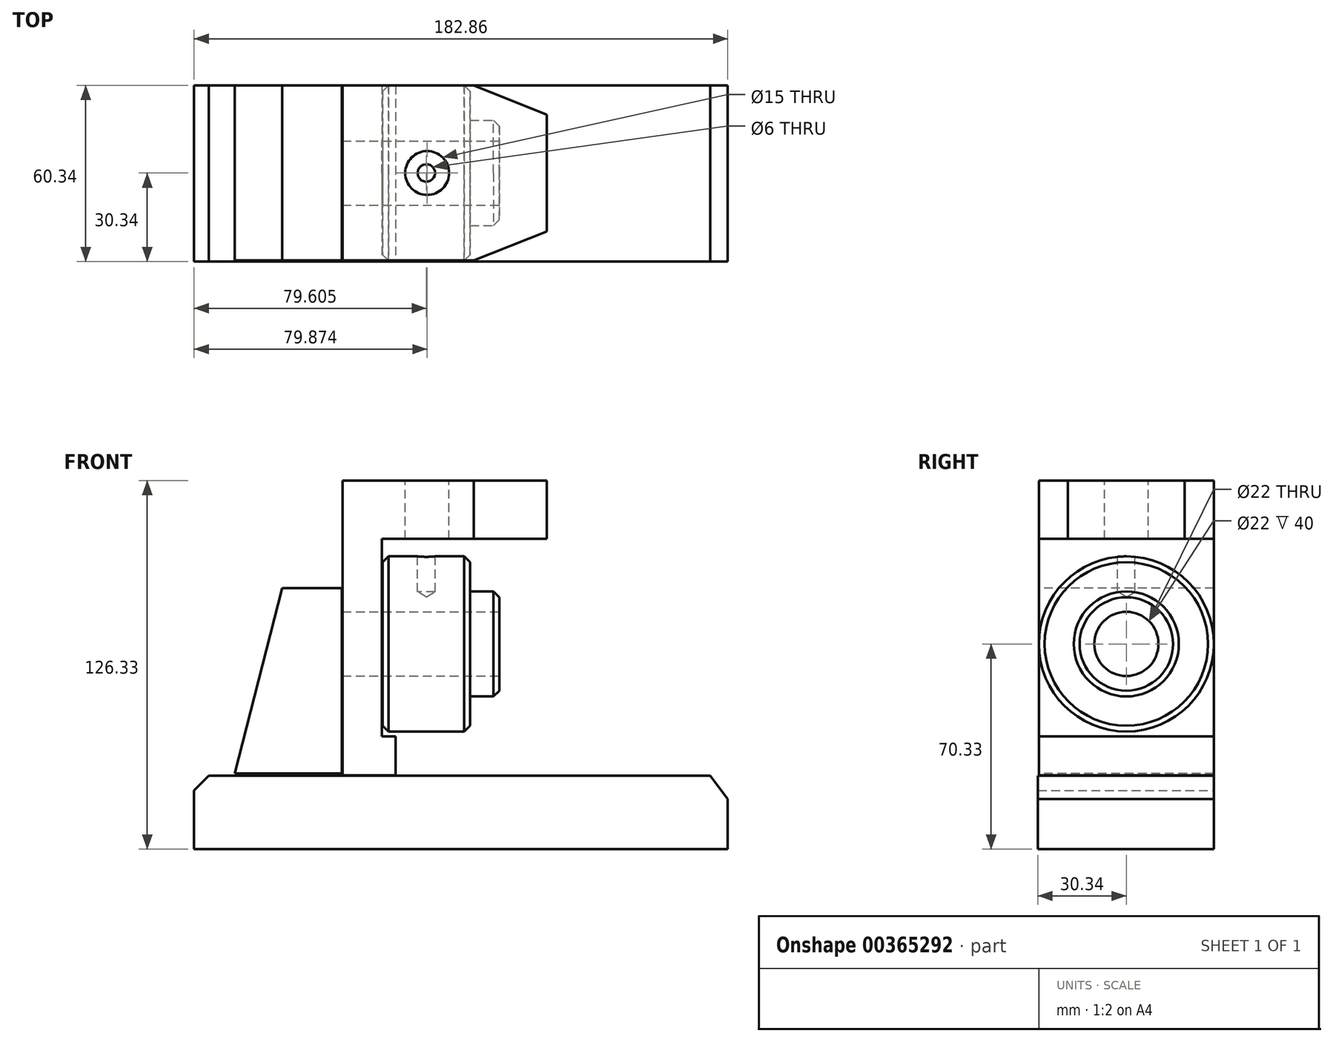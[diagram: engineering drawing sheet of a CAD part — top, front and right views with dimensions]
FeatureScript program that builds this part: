
annotation { "Feature Type Name" : "Feature", "Feature Type Description" : "" }
export const myFeature = defineFeature(function(context is Context, id is Id, definition is map)
    precondition{}
    {
        {
            var Q0;
            Q0=qCreatedBy(makeId("Front.planeOp"),FACE);
            var sketch = newSketch(context, id + "F0", { "sketchPlane" : qUnion([Q0])});
            skLineSegment(sketch, "E0", {"start": v(-19, 18) * mm, "end": v(-29, 18) * mm});
            skLineSegment(sketch, "E1", {"start": v(-29, 18) * mm, "end": v(-29, 30) * mm});
            skLineSegment(sketch, "E2", {"start": v(-29, 30) * mm, "end": v(-59, 30) * mm});
            skPoint(sketch, "E3", {"position": v(0, 0) * mm});
            skLineSegment(sketch, "E4", {"start": v(-19, 18) * mm, "end": v(-19, 11) * mm});
            skLineSegment(sketch, "E5", {"start": v(-19, 11) * mm, "end": v(-59, 11) * mm});
            skLineSegment(sketch, "E6", {"start": v(-59, 11) * mm, "end": v(-59, 30) * mm});
            skLineSegment(sketch, "E7", {"start": v(0, 0) * mm, "end": v(-59, 0) * mm, "construction": true});
            skSolve(sketch);
        }
        {
            var Q0;
            Q0=makeQuery(id+"F0.imprint","IMPRINT",FACE,{"disambiguationData":[TD([[makeQuery(id+"F0.imprint","IMPRINT",EDGE,{"derivedFrom":sQuery(id+"F0.wireOp",EDGE,"E0")}),1.0]])]});
            var Q1;
            Q1=sQuery(id+"F0.wireOp",EDGE,"E7");
            revolve(context, id + "F1", {"entities" : qUnion([Q0]), "axis" : qUnion([Q1]), "revolveType" : RevolveType.FULL});
        }
        {
            var Q0;
            Q0=makeQuery(id+"F1.opRevolve","SWEPT_EDGE",EDGE,{"disambiguationData":[OSD([sQuery(id+"F0.wireOp",EDGE,"E0"),sQuery(id+"F0.wireOp",EDGE,"E4")])]});
            var Q1;
            Q1=makeQuery(id+"F1.opRevolve","SWEPT_EDGE",EDGE,{"disambiguationData":[OSD([sQuery(id+"F0.wireOp",EDGE,"E1"),sQuery(id+"F0.wireOp",EDGE,"E2")])]});
            var Q2;
            Q2=makeQuery(id+"F1.opRevolve","SWEPT_EDGE",EDGE,{"disambiguationData":[OSD([sQuery(id+"F0.wireOp",EDGE,"E2"),sQuery(id+"F0.wireOp",EDGE,"E6")])]});
            chamfer(context, id + "F2", {"entities" : qUnion([Q0, Q1, Q2]), "width" : 2 * mm, "tangentPropagation" : true});
        }
        {
            var Q0;
            Q0=qCreatedBy(makeId("Top.planeOp"),FACE);
            cPlane(context, id + "F3", {"entities" : qUnion([Q0]), "cplaneType" : CPlaneType.OFFSET, "offset" : 30 * mm, "width" : 150 * mm, "height" : 150 * mm});
        }
        {
            var Q0;
            Q0=qCreatedBy(id+"F3.planeOp",FACE);
            var sketch = newSketch(context, id + "F4", { "sketchPlane" : qUnion([Q0])});
            skCircle(sketch, "E8", {"center": v(-44, 0) * mm, "radius": 3 * mm});
            skSolve(sketch);
        }
        {
            var Q0;
            Q0=sQuery(id+"F4.wireOp",VERTEX,"E8.center");
            var Q1;
            Q1=makeQuery(id+"F1.opRevolve","SWEPT_BODY",BODY,{"disambiguationData":[OSD([sQuery(id+"F0.wireOp",EDGE,"E0"),sQuery(id+"F0.wireOp",EDGE,"E1"),sQuery(id+"F0.wireOp",EDGE,"E2"),sQuery(id+"F0.wireOp",EDGE,"E4"),sQuery(id+"F0.wireOp",EDGE,"E5"),sQuery(id+"F0.wireOp",EDGE,"E6")])]});
            hole(context, id + "F5", {"style" : HoleStyle.SIMPLE, "endStyle" : HoleEndStyle.BLIND, "holeDiameter" : 6 * mm, "holeDepth" : 12 * mm, "isTappedThrough" : true, "tappedDepth" : 12 * mm, "tapClearance" : 3, "locations" : qUnion([Q0]), "scope" : qUnion([Q1])});
        }
        {
            var Q0;
            Q0=qCreatedBy(makeId("Right.planeOp"),FACE);
            cPlane(context, id + "F6", {"entities" : qUnion([Q0]), "cplaneType" : CPlaneType.OFFSET, "offset" : 59 * mm, "oppositeDirection" : true, "width" : 150 * mm, "height" : 150 * mm});
        }
        {
            var Q0;
            Q0=qCreatedBy(makeId("Front.planeOp"),FACE);
            cPlane(context, id + "F7", {"entities" : qUnion([Q0]), "cplaneType" : CPlaneType.OFFSET, "offset" : 30 * mm, "width" : 150 * mm, "height" : 150 * mm});
        }
        {
            var Q0;
            Q0=qCreatedBy(id+"F7.planeOp",FACE);
            var sketch = newSketch(context, id + "F8", { "sketchPlane" : qUnion([Q0])});
            skLineSegment(sketch, "E9", {"start": v(-59.2, 36) * mm, "end": v(-59.2, -31.66) * mm});
            skLineSegment(sketch, "E10", {"start": v(-59.2, -31.66) * mm, "end": v(-54.5, -31.66) * mm});
            skLineSegment(sketch, "E11", {"start": v(-54.5, -31.66) * mm, "end": v(-54.5, -45) * mm});
            skLineSegment(sketch, "E12", {"start": v(-54.5, -45) * mm, "end": v(-72.74, -45) * mm});
            skLineSegment(sketch, "E13", {"start": v(-72.74, -45) * mm, "end": v(-72.74, 56) * mm});
            skLineSegment(sketch, "E14", {"start": v(-72.74, 56) * mm, "end": v(-2.74, 56) * mm});
            skLineSegment(sketch, "E15", {"start": v(-2.74, 56) * mm, "end": v(-2.74, 36) * mm});
            skLineSegment(sketch, "E16", {"start": v(-2.74, 36) * mm, "end": v(-59.2, 36) * mm});
            skSolve(sketch);
        }
        {
            var Q0;
            Q0=makeQuery(id+"F8.imprint","IMPRINT",FACE,{"disambiguationData":[TD([[makeQuery(id+"F8.imprint","IMPRINT",EDGE,{"derivedFrom":sQuery(id+"F8.wireOp",EDGE,"E9")}),-1.0]])]});
            extrude(context, id + "F9", {"entities" : qUnion([Q0]), "oppositeDirection" : true, "depth" : 60 * mm});
        }
        {
            var Q0;
            Q0=makeQuery(id+"F9.opExtrude","CAP_EDGE",EDGE,{"disambiguationData":[OSD([sQuery(id+"F8.wireOp",EDGE,"E15")])],"isStart":false});
            var Q1;
            Q1=makeQuery(id+"F9.opExtrude","CAP_EDGE",EDGE,{"disambiguationData":[OSD([sQuery(id+"F8.wireOp",EDGE,"E15")])],"isStart":true});
            chamfer(context, id + "F10", {"entities" : qUnion([Q0, Q1]), "chamferType" : ChamferType.TWO_OFFSETS, "width1" : 25 * mm, "oppositeDirection" : false, "width2" : 10 * mm, "tangentPropagation" : true});
        }
        {
            var Q0;
            Q0=qCreatedBy(id+"F3.planeOp",FACE);
            cPlane(context, id + "F11", {"entities" : qUnion([Q0]), "cplaneType" : CPlaneType.OFFSET, "offset" : 25 * mm, "width" : 150 * mm, "height" : 150 * mm});
        }
        {
            var Q0;
            Q0=makeQuery(id+"F9.opExtrude","SWEPT_FACE",FACE,{"disambiguationData":[OSD([sQuery(id+"F8.wireOp",EDGE,"E14")])]});
            var sketch = newSketch(context, id + "F12", { "sketchPlane" : qUnion([Q0])});
            skPoint(sketch, "E17", {"position": v(-43.74, 0) * mm});
            skSolve(sketch);
        }
        {
            var Q0;
            Q0=sQuery(id+"F12.wireOp",VERTEX,"E17");
            var Q1;
            Q1=makeQuery(id+"F9.opExtrude","SWEPT_BODY",BODY,{"disambiguationData":[OSD([sQuery(id+"F8.wireOp",EDGE,"E9"),sQuery(id+"F8.wireOp",EDGE,"E10"),sQuery(id+"F8.wireOp",EDGE,"E11"),sQuery(id+"F8.wireOp",EDGE,"E12"),sQuery(id+"F8.wireOp",EDGE,"E13"),sQuery(id+"F8.wireOp",EDGE,"E14"),sQuery(id+"F8.wireOp",EDGE,"E15"),sQuery(id+"F8.wireOp",EDGE,"E16")])]});
            hole(context, id + "F13", {"style" : HoleStyle.SIMPLE, "endStyle" : HoleEndStyle.THROUGH, "holeDiameter" : 15 * mm, "isTappedThrough" : true, "tappedDepth" : 12 * mm, "tapClearance" : 3, "locations" : qUnion([Q0]), "scope" : qUnion([Q1])});
        }
        {
            var Q0;
            Q0=qCreatedBy(id+"F6.planeOp",FACE);
            var sketch = newSketch(context, id + "F14", { "sketchPlane" : qUnion([Q0])});
            skPoint(sketch, "E18", {"position": v(0, 0) * mm});
            skSolve(sketch);
        }
        {
            var Q0;
            Q0=sQuery(id+"F14.wireOp",VERTEX,"E18");
            var Q1;
            Q1=makeQuery(id+"F9.opExtrude","SWEPT_BODY",BODY,{"disambiguationData":[OSD([sQuery(id+"F8.wireOp",EDGE,"E9"),sQuery(id+"F8.wireOp",EDGE,"E10"),sQuery(id+"F8.wireOp",EDGE,"E11"),sQuery(id+"F8.wireOp",EDGE,"E12"),sQuery(id+"F8.wireOp",EDGE,"E13"),sQuery(id+"F8.wireOp",EDGE,"E14"),sQuery(id+"F8.wireOp",EDGE,"E15"),sQuery(id+"F8.wireOp",EDGE,"E16")])]});
            hole(context, id + "F15", {"style" : HoleStyle.SIMPLE, "endStyle" : HoleEndStyle.THROUGH, "holeDiameter" : 22 * mm, "isTappedThrough" : true, "tappedDepth" : 12 * mm, "tapClearance" : 3, "locations" : qUnion([Q0]), "scope" : qUnion([Q1])});
        }
        {
            var Q0;
            Q0=qCreatedBy(id+"F7.planeOp",FACE);
            var sketch = newSketch(context, id + "F16", { "sketchPlane" : qUnion([Q0])});
            skLineSegment(sketch, "E19", {"start": v(-54.13, -45.18) * mm, "end": v(59.25, -45.18) * mm});
            skLineSegment(sketch, "E20", {"start": v(59.25, -45.18) * mm, "end": v(59.25, -70.33) * mm});
            skLineSegment(sketch, "E21", {"start": v(59.25, -70.33) * mm, "end": v(-123.61, -70.33) * mm});
            skLineSegment(sketch, "E22", {"start": v(-123.61, -70.33) * mm, "end": v(-123.61, -45.18) * mm});
            skLineSegment(sketch, "E23", {"start": v(-123.61, -45.18) * mm, "end": v(-54.13, -45.18) * mm});
            skSolve(sketch);
        }
        {
            var Q0;
            Q0=makeQuery(id+"F16.imprint","IMPRINT",FACE,{"disambiguationData":[TD([[makeQuery(id+"F16.imprint","IMPRINT",EDGE,{"derivedFrom":sQuery(id+"F16.wireOp",EDGE,"E19")}),-1.0]])]});
            var Q1;
            Q1=makeQuery(id+"F9.opExtrude","SWEPT_BODY",BODY,{"disambiguationData":[OSD([sQuery(id+"F8.wireOp",EDGE,"E9"),sQuery(id+"F8.wireOp",EDGE,"E10"),sQuery(id+"F8.wireOp",EDGE,"E11"),sQuery(id+"F8.wireOp",EDGE,"E12"),sQuery(id+"F8.wireOp",EDGE,"E13"),sQuery(id+"F8.wireOp",EDGE,"E14"),sQuery(id+"F8.wireOp",EDGE,"E15"),sQuery(id+"F8.wireOp",EDGE,"E16")])]});
            extrude(context, id + "F17", {"entities" : qUnion([Q0]), "oppositeDirection" : true, "endBoundEntityBody" : qUnion([Q1]), "depth" : 60 * mm, "hasSecondDirection" : true, "secondDirectionOppositeDirection" : false, "secondDirectionDepth" : 0.34 * mm});
        }
        {
            var Q0;
            Q0=qCreatedBy(id+"F7.planeOp",FACE);
            var sketch = newSketch(context, id + "F18", { "sketchPlane" : qUnion([Q0])});
            skLineSegment(sketch, "E24", {"start": v(-109.65, -44.34) * mm, "end": v(-93.44, 19.07) * mm});
            skLineSegment(sketch, "E25", {"start": v(-93.44, 19.07) * mm, "end": v(-72.94, 19.07) * mm});
            skLineSegment(sketch, "E26", {"start": v(-72.94, 19.07) * mm, "end": v(-72.94, -44.34) * mm});
            skLineSegment(sketch, "E27", {"start": v(-72.94, -44.34) * mm, "end": v(-109.65, -44.34) * mm});
            skPoint(sketch, "E28.start.orphan", {"position": v(0, -56.98) * mm});
            skSolve(sketch);
        }
        {
            var Q0;
            Q0=makeQuery(id+"F18.imprint","IMPRINT",FACE,{"disambiguationData":[TD([[makeQuery(id+"F18.imprint","IMPRINT",EDGE,{"derivedFrom":sQuery(id+"F18.wireOp",EDGE,"E24")}),-1.0]])]});
            extrude(context, id + "F19", {"entities" : qUnion([Q0]), "oppositeDirection" : true, "depth" : 60 * mm});
        }
        {
            var Q0;
            Q0=makeQuery(id+"F17.opExtrude","SWEPT_EDGE",EDGE,{"disambiguationData":[OSD([sQuery(id+"F16.wireOp",EDGE,"E22"),sQuery(id+"F16.wireOp",EDGE,"E23")])]});
            chamfer(context, id + "F20", {"entities" : qUnion([Q0]), "width" : 5 * mm, "tangentPropagation" : true});
        }
        {
            var Q0;
            Q0=makeQuery(id+"F17.opExtrude","SWEPT_EDGE",EDGE,{"disambiguationData":[OSD([sQuery(id+"F16.wireOp",EDGE,"E19"),sQuery(id+"F16.wireOp",EDGE,"E20")])]});
            chamfer(context, id + "F21", {"entities" : qUnion([Q0]), "chamferType" : ChamferType.TWO_OFFSETS, "width1" : 8 * mm, "oppositeDirection" : false, "width2" : 6 * mm, "tangentPropagation" : true});
        }
    });
